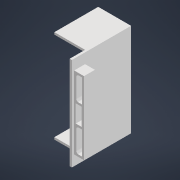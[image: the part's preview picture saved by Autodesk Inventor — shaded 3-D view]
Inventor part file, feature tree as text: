
AUTODESK INVENTOR PART (.ipt)
format: ipt  version: 2022 (Build 260153000, 153)  size: 184,320 bytes
history: native  units: mm
features: other x4, extrude x3, reference x3, sketch x2, projected_geometry x1
ambient origin geometry x8: Origin, YZ Plane, XZ Plane, XY Plane, X Axis, Y Axis, Z Axis, Center Point
bodies: Solid1 (feature_tree)
feature tree (13):
  extrude  "Extrusion1"  Depth=2.0mm
  sketch  "Sketch10"  dims[d2=6.0mm d3=0.1mm d4=10.0mm d5=0.0mm d64=81.0mm d65=90.0deg d66=2.0mm d67=40.0mm d68=2.0mm d69=2.0mm d70=0.0mm d71=30.0mm d72=0.0mm d6=0.5mm d7=0.872665mm d28=0.5mm d29=0.872665mm d30=0.5mm d31=0.872665mm]
  extrude  "Extrusion9"  Depth=0.1mm
  extrude  "Extrusion10"  Depth=10.0mm TaperAngle=0.0deg
  sketch  "Sketch1"  dims[d0=2.0mm d1=2.0mm]
  reference  "Reference1"
  reference  "Reference2"
  reference  "Reference3"
  projected_geometry  "Projected Loop9"
  other  "<userpath>\OneDrive\Namizje\school\3. letnik\ZOPp\laserski merilnik\3d model\Assembly1.iam"
  other  "Assembly1.iam"
  other  "Hold of motors:1"
  other  "zaponka za motor2:1"
